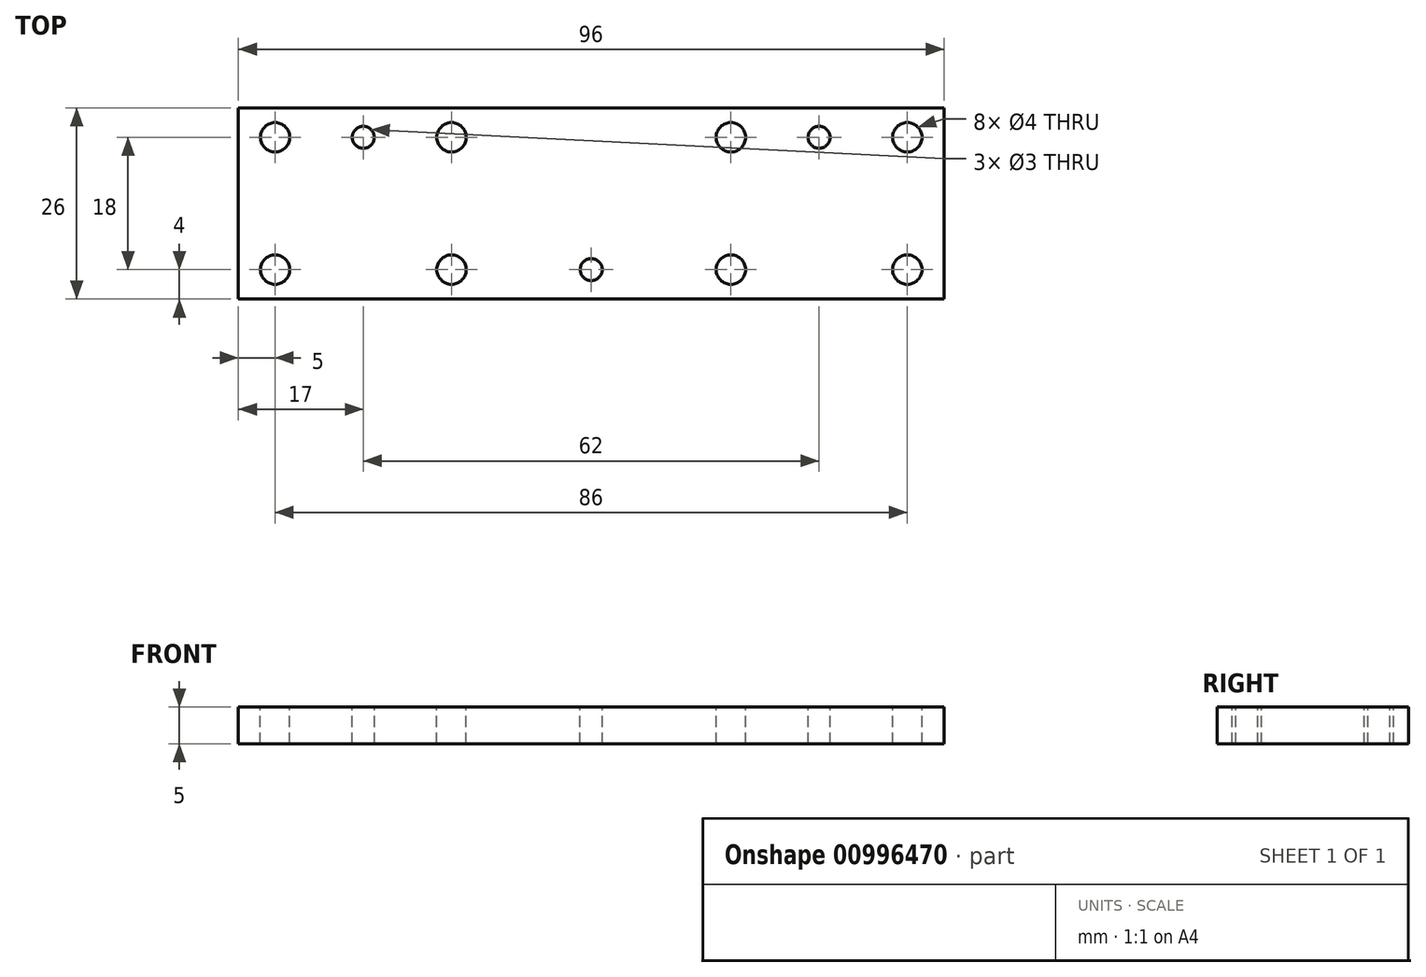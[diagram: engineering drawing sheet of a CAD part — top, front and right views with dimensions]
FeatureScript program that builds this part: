
annotation { "Feature Type Name" : "Feature", "Feature Type Description" : "" }
export const myFeature = defineFeature(function(context is Context, id is Id, definition is map)
    precondition{}
    {
        {
            var Q0;
            Q0=qCreatedBy(makeId("Top.planeOp"),FACE);
            var sketch = newSketch(context, id + "F0", { "sketchPlane" : qUnion([Q0])});
            skLineSegment(sketch, "E0.bottom", {"start": v(-48, 13) * mm, "end": v(48, 13) * mm});
            skLineSegment(sketch, "E0.top", {"start": v(-48, -13) * mm, "end": v(48, -13) * mm});
            skLineSegment(sketch, "E0.left", {"start": v(-48, 13) * mm, "end": v(-48, -13) * mm});
            skLineSegment(sketch, "E0.right", {"start": v(48, 13) * mm, "end": v(48, -13) * mm});
            skLineSegment(sketch, "E1", {"start": v(0, 13) * mm, "end": v(0, -13) * mm, "construction": true});
            skLineSegment(sketch, "E2", {"start": v(48, 0) * mm, "end": v(-48, 0) * mm, "construction": true});
            skSolve(sketch);
        }
        {
            var Q0;
            Q0=makeQuery(id+"F0.imprint","IMPRINT",FACE,{"disambiguationData":[TD([[makeQuery(id+"F0.imprint","IMPRINT",EDGE,{"derivedFrom":sQuery(id+"F0.wireOp",EDGE,"E0.bottom")}),-1.0]])]});
            extrude(context, id + "F1", {"entities" : qUnion([Q0]), "depth" : 5 * mm, "offsetDistance" : 25 * mm});
        }
        {
            var Q0;
            Q0=makeQuery(id+"F1.opExtrude","CAP_FACE",FACE,{"disambiguationData":[OSD([sQuery(id+"F0.wireOp",EDGE,"E0.bottom"),sQuery(id+"F0.wireOp",EDGE,"E0.top"),sQuery(id+"F0.wireOp",EDGE,"E0.left"),sQuery(id+"F0.wireOp",EDGE,"E0.right")])],"isStart":false});
            var sketch = newSketch(context, id + "F2", { "sketchPlane" : qUnion([Q0])});
            skLineSegment(sketch, "E3", {"start": v(0, 13) * mm, "end": v(0, -13) * mm, "construction": true});
            skLineSegment(sketch, "E4", {"start": v(48, 0) * mm, "end": v(-48, 0) * mm, "construction": true});
            skPoint(sketch, "E5", {"position": v(-43, 9) * mm});
            skPoint(sketch, "E6", {"position": v(-19, 9) * mm});
            skPoint(sketch, "E7", {"position": v(-43, -9) * mm});
            skPoint(sketch, "E8", {"position": v(-19, -9) * mm});
            skPoint(sketch, "E9", {"position": v(19, 9) * mm});
            skPoint(sketch, "E10", {"position": v(43, 9) * mm});
            skPoint(sketch, "E11", {"position": v(43, -9) * mm});
            skPoint(sketch, "E12", {"position": v(19, -9) * mm});
            skLineSegment(sketch, "E13.bottom", {"start": v(-48, 13) * mm, "end": v(48, 13) * mm});
            skLineSegment(sketch, "E13.top", {"start": v(-48, -13) * mm, "end": v(48, -13) * mm});
            skLineSegment(sketch, "E13.left", {"start": v(-48, 13) * mm, "end": v(-48, -13) * mm});
            skLineSegment(sketch, "E13.right", {"start": v(48, 13) * mm, "end": v(48, -13) * mm});
            skSolve(sketch);
        }
        {
            var Q0;
            Q0=sQuery(id+"F2.wireOp",VERTEX,"E5");
            var Q1;
            Q1=sQuery(id+"F2.wireOp",VERTEX,"E6");
            var Q2;
            Q2=sQuery(id+"F2.wireOp",VERTEX,"E9");
            var Q3;
            Q3=sQuery(id+"F2.wireOp",VERTEX,"E10");
            var Q4;
            Q4=sQuery(id+"F2.wireOp",VERTEX,"E11");
            var Q5;
            Q5=sQuery(id+"F2.wireOp",VERTEX,"E12");
            var Q6;
            Q6=sQuery(id+"F2.wireOp",VERTEX,"E8");
            var Q7;
            Q7=sQuery(id+"F2.wireOp",VERTEX,"E7");
            var Q8;
            Q8=makeQuery(id+"F1.opExtrude","SWEPT_BODY",BODY,{"disambiguationData":[OSD([sQuery(id+"F0.wireOp",EDGE,"E0.bottom"),sQuery(id+"F0.wireOp",EDGE,"E0.top"),sQuery(id+"F0.wireOp",EDGE,"E0.left"),sQuery(id+"F0.wireOp",EDGE,"E0.right")])]});
            hole(context, id + "F3", {"style" : HoleStyle.SIMPLE, "endStyle" : HoleEndStyle.THROUGH, "holeDiameter" : 4 * mm, "majorDiameter" : 5 * mm, "isTappedThrough" : true, "tappedDepth" : 12 * mm, "tapClearance" : 3, "locations" : qUnion([Q0, Q1, Q2, Q3, Q4, Q5, Q6, Q7]), "scope" : qUnion([Q8])});
        }
        {
            var Q0;
            Q0=makeQuery(id+"F1.opExtrude","CAP_FACE",FACE,{"disambiguationData":[OSD([sQuery(id+"F0.wireOp",EDGE,"E0.bottom"),sQuery(id+"F0.wireOp",EDGE,"E0.top"),sQuery(id+"F0.wireOp",EDGE,"E0.left"),sQuery(id+"F0.wireOp",EDGE,"E0.right")])],"isStart":false});
            var sketch = newSketch(context, id + "F4", { "sketchPlane" : qUnion([Q0])});
            skLineSegment(sketch, "E14.bottom", {"start": v(-48, 13) * mm, "end": v(48, 13) * mm});
            skLineSegment(sketch, "E14.top", {"start": v(-48, -13) * mm, "end": v(48, -13) * mm});
            skLineSegment(sketch, "E14.left", {"start": v(-48, 13) * mm, "end": v(-48, -13) * mm});
            skLineSegment(sketch, "E14.right", {"start": v(48, 13) * mm, "end": v(48, -13) * mm});
            skLineSegment(sketch, "E15", {"start": v(0, 13) * mm, "end": v(0, -13) * mm, "construction": true});
            skLineSegment(sketch, "E16", {"start": v(-48, 0) * mm, "end": v(48, 0) * mm, "construction": true});
            skPoint(sketch, "E17", {"position": v(0, -9) * mm});
            skLineSegment(sketch, "E18", {"start": v(-43, 9) * mm, "end": v(-19, 9) * mm, "construction": true});
            skLineSegment(sketch, "E19", {"start": v(-31, 3.6) * mm, "end": v(-31, 14.4) * mm, "construction": true});
            skPoint(sketch, "E20", {"position": v(-31, 9) * mm});
            skPoint(sketch, "E21", {"position": v(31, 9) * mm});
            skSolve(sketch);
        }
        {
            var Q0;
            Q0=sQuery(id+"F4.wireOp",VERTEX,"E20");
            var Q1;
            Q1=sQuery(id+"F4.wireOp",VERTEX,"E17");
            var Q2;
            Q2=sQuery(id+"F4.wireOp",VERTEX,"E21");
            var Q3;
            Q3=makeQuery(id+"F1.opExtrude","SWEPT_BODY",BODY,{"disambiguationData":[OSD([sQuery(id+"F0.wireOp",EDGE,"E0.bottom"),sQuery(id+"F0.wireOp",EDGE,"E0.top"),sQuery(id+"F0.wireOp",EDGE,"E0.left"),sQuery(id+"F0.wireOp",EDGE,"E0.right")])]});
            hole(context, id + "F5", {"style" : HoleStyle.SIMPLE, "endStyle" : HoleEndStyle.THROUGH, "holeDiameter" : 3 * mm, "majorDiameter" : 5 * mm, "isTappedThrough" : true, "tappedDepth" : 12 * mm, "tapClearance" : 3, "locations" : qUnion([Q0, Q1, Q2]), "scope" : qUnion([Q3])});
        }
    });
